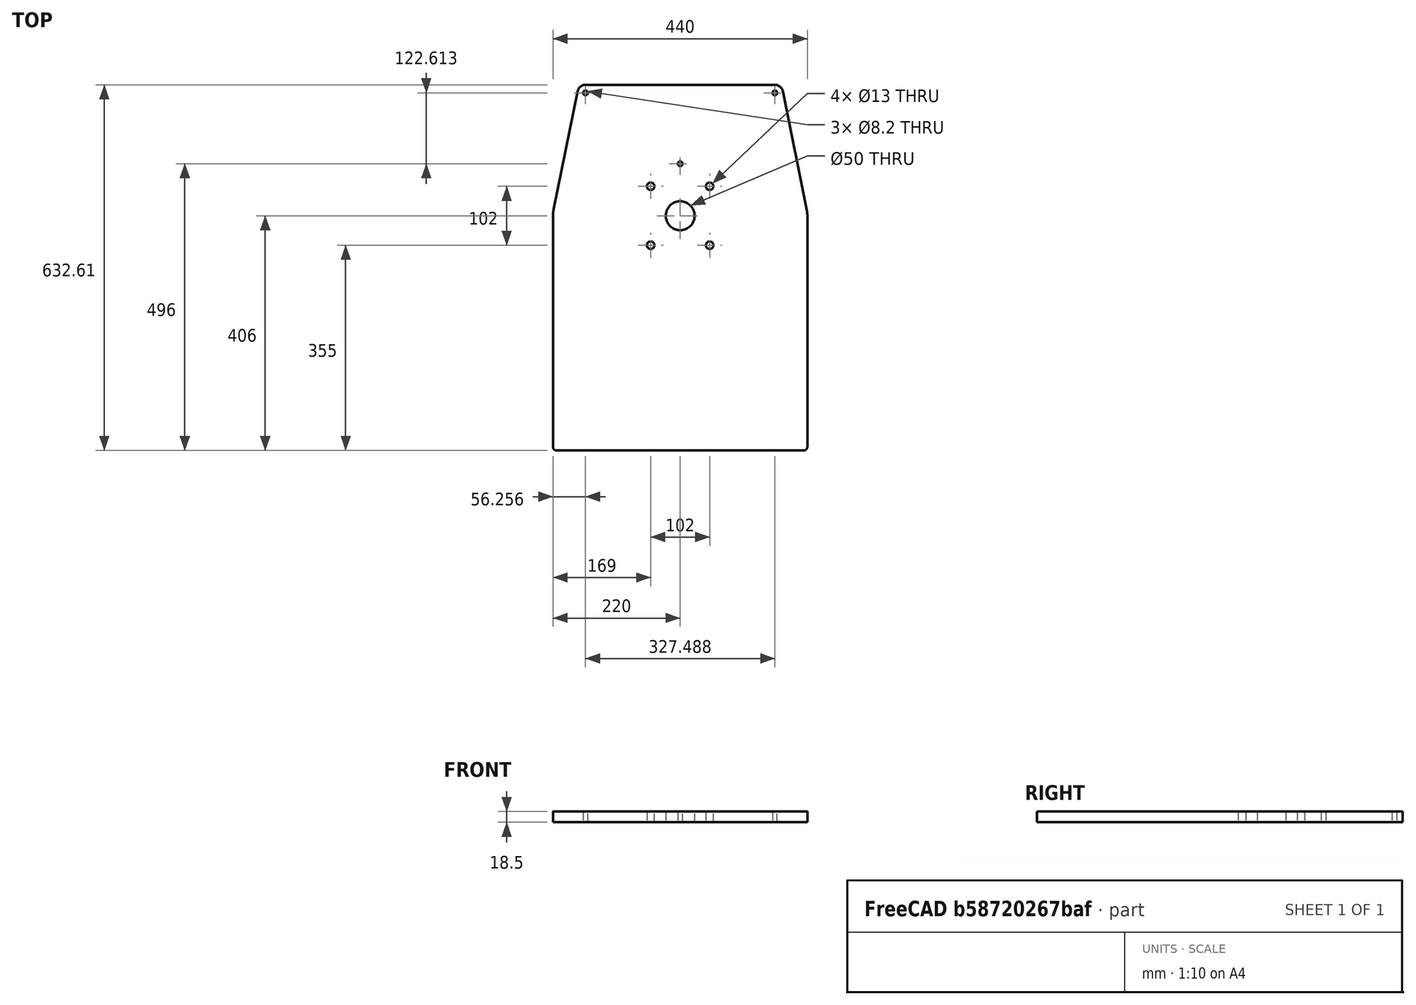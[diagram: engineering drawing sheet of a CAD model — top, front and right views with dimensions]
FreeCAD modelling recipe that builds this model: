
FCSTD DOCUMENT  (FreeCAD 0.20R29410 (Git))
Label: ComputerPlatform
License: All rights reserved
LicenseURL: http://en.wikipedia.org/wiki/All_rights_reserved
objects: App::DocumentObjectGroup×3, PartDesign::CoordinateSystem×2, Sketcher::SketchObject×1, PartDesign::Pad×1, PartDesign::Body×1, App::FeaturePython×1, App::Part×1
note: 6 computed .brp shape members not serialized (recipe doc carries the construction recipe); baked Part::Feature solids carry a one-line shape summary decoded from their .brp
EXTERNAL_REF file=DrivePlatform.FCStd obj=Sketch
EXTERNAL_REF file=Params.FCStd obj=Spreadsheet

FEATURE [Sketcher::SketchObject] Sketch
  FullyConstrained = true
  MapMode = 5
  Support = -> [XY_Plane]
  expr: Constraints[57] = <<DrivePlatform>>#<<Sketch>>.Constraints.DriveAdjSpacingX
  expr: Constraints[58] = <<DrivePlatform>>#<<Sketch>>.Constraints.DriveAdjSpacingY
  expr: Constraints[59] = <<Params>>#<<Params>>.DriveAdjMiddleOffset
  sketch-geometry (30):
    g0: LineSegment StartX=-220 StartY=6.1e-15 StartZ=0 EndX=-220 EndY=-400 EndZ=0
    g1: LineSegment StartX=-214 StartY=-406 StartZ=0 EndX=214 EndY=-406 EndZ=0
    g2: LineSegment StartX=220 StartY=-400 StartZ=0 EndX=220 EndY=0 EndZ=0
    g3: Circle CenterX=0 CenterY=0 CenterZ=0 NormalX=0 NormalY=0 NormalZ=1 AngleXU=0 Radius=25
    g4: Circle CenterX=51 CenterY=51 CenterZ=0 NormalX=0 NormalY=0 NormalZ=1 AngleXU=0 Radius=6.5
    g5: Circle CenterX=-51 CenterY=51 CenterZ=0 NormalX=0 NormalY=0 NormalZ=1 AngleXU=0 Radius=6.5
    g6: Circle CenterX=-51 CenterY=-51 CenterZ=0 NormalX=0 NormalY=0 NormalZ=1 AngleXU=0 Radius=6.5
    g7: Circle CenterX=51 CenterY=-51 CenterZ=0 NormalX=0 NormalY=0 NormalZ=1 AngleXU=0 Radius=6.5
    g8: LineSegment StartX=51 StartY=51 StartZ=0 EndX=51 EndY=-51 EndZ=0
    g9: LineSegment StartX=51 StartY=51 StartZ=0 EndX=-51 EndY=51 EndZ=0
    g10: ArcOfCircle CenterX=214 CenterY=-400 CenterZ=0 NormalX=0 NormalY=0 NormalZ=1 AngleXU=0 Radius=6 StartAngle=4.71239 EndAngle=6.28319
    g11: GeomPoint X=220 Y=-406 Z=0
    g12: ArcOfCircle CenterX=-214 CenterY=-400 CenterZ=0 NormalX=0 NormalY=0 NormalZ=1 AngleXU=0 Radius=6 StartAngle=3.14159 EndAngle=4.71239
    g13: GeomPoint X=-220 Y=-406 Z=0
    g14: ArcOfCircle CenterX=-170 CenterY=0 CenterZ=0 NormalX=0 NormalY=0 NormalZ=1 AngleXU=0 Radius=50 StartAngle=2.94211 EndAngle=3.14159
    g15: ArcOfCircle CenterX=170 CenterY=0 CenterZ=0 NormalX=0 NormalY=0 NormalZ=1 AngleXU=0 Radius=50 StartAngle=0 EndAngle=0.199484
    g16: GeomPoint X=0 Y=-406 Z=0
    g17: LineSegment StartX=-219.008 StartY=9.90816 StartZ=0 EndX=-177.466 EndY=215.387 EndZ=0
    g18: LineSegment StartX=219.008 StartY=9.90816 StartZ=0 EndX=177.466 EndY=215.387 EndZ=0
    g19: Circle CenterX=0 CenterY=90 CenterZ=0 NormalX=0 NormalY=0 NormalZ=1 AngleXU=0 Radius=4.1
    g20: Circle CenterX=163.744 CenterY=212.613 CenterZ=0 NormalX=0 NormalY=0 NormalZ=1 AngleXU=0 Radius=4.1
    g21: Circle CenterX=-163.744 CenterY=212.613 CenterZ=0 NormalX=0 NormalY=0 NormalZ=1 AngleXU=0 Radius=4.1
    g22: LineSegment StartX=-163.744 StartY=226.613 StartZ=0 EndX=163.744 EndY=226.613 EndZ=0
    g23: GeomPoint X=0 Y=226.613 Z=0
    g24: LineSegment StartX=-163.744 StartY=212.613 StartZ=0 EndX=0 EndY=212.613 EndZ=0
    g25: LineSegment StartX=0 StartY=212.613 StartZ=0 EndX=163.744 EndY=212.613 EndZ=0
    g26: ArcOfCircle CenterX=163.744 CenterY=212.613 CenterZ=0 NormalX=0 NormalY=0 NormalZ=1 AngleXU=0 Radius=14 StartAngle=0.199484 EndAngle=1.5708
    g27: GeomPoint X=175.197 Y=226.613 Z=0
    g28: ArcOfCircle CenterX=-163.744 CenterY=212.613 CenterZ=0 NormalX=0 NormalY=0 NormalZ=1 AngleXU=0 Radius=14 StartAngle=1.5708 EndAngle=2.94211
    g29: GeomPoint X=-175.197 Y=226.613 Z=0
  constraints (70):
    c: Vertical(g0)
    c: Horizontal(g1)
    c: Vertical(g2)
    c: DistanceX(g13,g11) = 440
    c: Diameter(g3) = 50
    c: Coincident(g8,g4)
    c: Coincident(g8,g7)
    c: Coincident(g9,g4)
    c: Coincident(g9,g5)
    c: Equal(g9,g8)
    c: Vertical(g8)
    c: Horizontal(g9)
    c: Equal(g4,g5)
    c: Equal(g5,g6)
    c: Equal(g6,g7)
    c: Diameter(g4) = 13
    c: DistanceY(g8,g8) = 102
    c: PointOnObject(g11,g2)
    c: PointOnObject(g11,g1)
    c: Tangent(g2,g10) = -1.5708
    c: Tangent(g1,g10) = -1.5708
    c: PointOnObject(g13,g0)
    c: PointOnObject(g13,g1)
    c: Tangent(g0,g12) = -1.5708
    c: Tangent(g1,g12) = -1.5708
    c: Equal(g12,g10)
    c: Radius(g10) = 6
    c: Coincident(g3,g-1)
    c: Symmetric(g7,g5,g3)
    c: Symmetric(g6,g4,g3)
    c: PointOnObject(g2,g-1)
    c: PointOnObject(g0,g-1)
    c: PointOnObject(g14,g-1)
    c: Coincident(g14,g0)
    c: PointOnObject(g15,g-1)
    c: Coincident(g15,g2)
    c: PointOnObject(g16,g-2)
    c: Symmetric(g1,g1,g16)
    c: DistanceY(g0,g0) = 400
    c: Equal(g14,g15)
    c: Radius(g15) = 50
    c: Tangent(g18,g15) = -1.5708
    c: Tangent(g17,g14) = 1.5708
    c: PointOnObject(g19,g-2)
    c: Equal(g21,g20)
    c: Equal(g20,g19)
    c: Diameter(g19) = 8.2
    c: Horizontal(g22)
    c: Symmetric(g29,g27,g23)
    c: PointOnObject(g23,g-2)
    c: Coincident(g24,g21)
    c: Horizontal(g24)
    c: Coincident(g25,g24)
    c: Horizontal(g25)
    c: Coincident(g25,g20)
    c: Equal(g24,g25)
    c: PointOnObject(g24,g-2)
    c: DistanceX(g21,g20) = 327.488
    c: DistanceY(g19,g21) = 122.613
    c: DistanceY(g3,g19) = 90
    c: PointOnObject(g27,g18)
    c: PointOnObject(g27,g22)
    c: Tangent(g18,g26) = -1.5708
    c: Tangent(g22,g26) = 1.5708
    c: PointOnObject(g29,g22)
    c: Tangent(g22,g28) = 1.5708
    c: Tangent(g17,g28) = 1.5708
    c: Coincident(g28,g21)
    c: Coincident(g26,g20)
    c: Radius(g26) = 14
FEATURE [PartDesign::Pad] Pad
  Direction = (0,0,1)
  Length = 18.5
  Length2 = 10
  Profile = -> Sketch
  ReferenceAxis = -> Sketch [N_Axis]
  Type = 0
  expr: Length = <<Params>>#<<Params>>.PlywoodThickness
FEATURE [PartDesign::Body] Body
  Group = -> [Sketch,Pad]
  Origin = -> Origin
  Tip = -> Pad
FEATURE [App::DocumentObjectGroup] Parts
FEATURE [PartDesign::CoordinateSystem] LCS_Origin
  AttacherType = Attacher::AttachEngine3D
  MapMode = 2
  Support = -> [X_Axis001]
FEATURE [App::FeaturePython] Variables  # WARN: FeaturePython — macro-defined, semantics opaque (R4)
  Type = App::PropertyContainer
FEATURE [App::DocumentObjectGroup] Constraints
FEATURE [App::DocumentObjectGroup] Configurations
FEATURE [PartDesign::CoordinateSystem] LCS_TopPivot
  AttacherType = Attacher::AttachEngine3D
  AttachmentOffset = pos=(0,0,18.5) rot=(0,0,1;0rad)
  MapMode = 2
  Placement = pos=(0,0,18.5) rot=(0,0,1;0rad)
  Support = -> [LCS_Origin]
  expr: .AttachmentOffset.Base.z = <<Pad>>.Length
FEATURE [App::Part] Assembly
  AssemblyType = Part::Link
  Group = -> [LCS_Origin,Variables,Constraints,Configurations,Body,LCS_TopPivot]
  Origin = -> Origin001
  Type = Assembly
